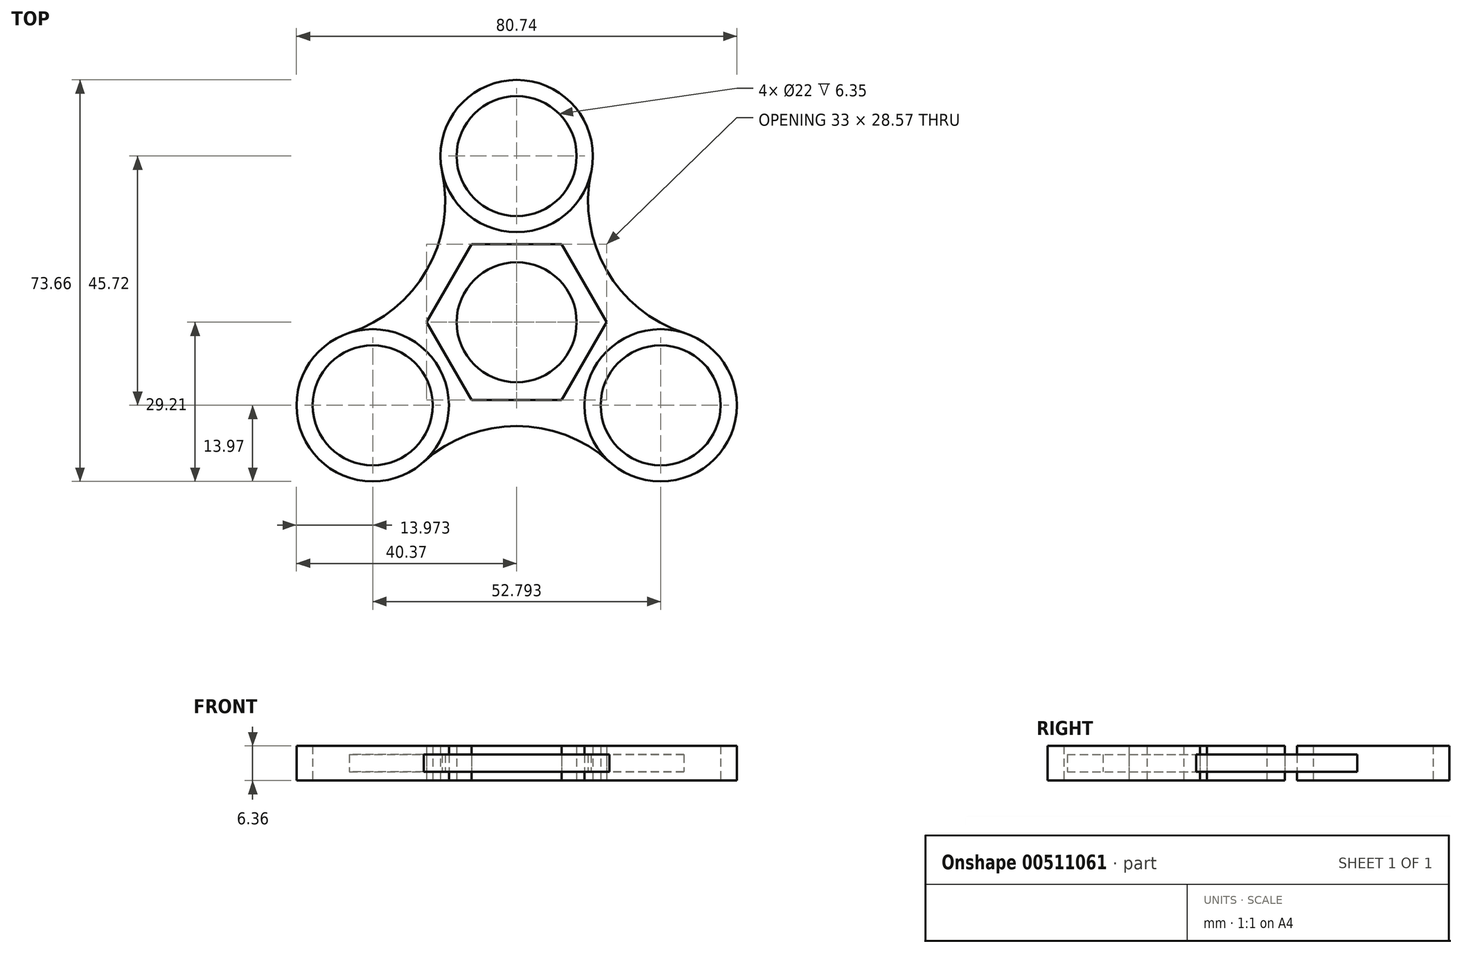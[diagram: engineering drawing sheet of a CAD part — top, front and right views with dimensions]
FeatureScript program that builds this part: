
annotation { "Feature Type Name" : "Feature", "Feature Type Description" : "" }
export const myFeature = defineFeature(function(context is Context, id is Id, definition is map)
    precondition{}
    {
        {
            var Q0;
            Q0=qCreatedBy(makeId("Top.planeOp"),FACE);
            var sketch = newSketch(context, id + "F0", { "sketchPlane" : qUnion([Q0])});
            skCircle(sketch, "E0", {"center": v(0, 0) * mm, "radius": 11 * mm});
            skCircle(sketch, "E1", {"center": v(0, 0) * mm, "radius": 44.45 * mm});
            skCircle(sketch, "E2", {"center": v(0, 30.48) * mm, "radius": 11 * mm});
            skCircle(sketch, "E3.1.0", {"center": v(-26.4, -15.24) * mm, "radius": 11 * mm});
            skCircle(sketch, "E3.2.0", {"center": v(26.4, -15.24) * mm, "radius": 11 * mm});
            skCircle(sketch, "E4", {"center": v(0, 30.48) * mm, "radius": 13.97 * mm});
            skCircle(sketch, "E5", {"center": v(26.4, -15.24) * mm, "radius": 13.97 * mm});
            skCircle(sketch, "E6", {"center": v(-26.4, -15.24) * mm, "radius": 13.97 * mm});
            skCircle(sketch, "E7.cCircle", {"center": v(0, 0) * mm, "radius": 14.29 * mm, "construction": true});
            skLineSegment(sketch, "E7.0", {"start": v(-8.25, 14.29) * mm, "end": v(8.25, 14.29) * mm});
            skLineSegment(sketch, "E7.1", {"start": v(8.25, 14.29) * mm, "end": v(16.5, 0) * mm});
            skLineSegment(sketch, "E7.2", {"start": v(16.5, 0) * mm, "end": v(8.25, -14.29) * mm});
            skLineSegment(sketch, "E7.3", {"start": v(8.25, -14.29) * mm, "end": v(-8.25, -14.29) * mm});
            skLineSegment(sketch, "E7.4", {"start": v(-8.25, -14.29) * mm, "end": v(-16.5, 0) * mm});
            skLineSegment(sketch, "E7.5", {"start": v(-16.5, 0) * mm, "end": v(-8.25, 14.29) * mm});
            skPoint(sketch, "E7.0.midPoint", {"position": v(0, 14.29) * mm});
            skSolve(sketch);
        }
        {
            var Q0;
            Q0=makeQuery(id+"F0.imprint","IMPRINT",FACE,{"disambiguationData":[TD([[makeQuery(id+"F0.imprint","IMPRINT",EDGE,{"derivedFrom":sQuery(id+"F0.wireOp",EDGE,"E2")}),-1.0]])]});
            var Q1;
            Q1=makeQuery(id+"F0.imprint","IMPRINT",FACE,{"disambiguationData":[TD([[makeQuery(id+"F0.imprint","IMPRINT",EDGE,{"derivedFrom":sQuery(id+"F0.wireOp",EDGE,"E0")}),-1.0]])]});
            var Q2;
            Q2=makeQuery(id+"F0.imprint","IMPRINT",FACE,{"disambiguationData":[TD([[makeQuery(id+"F0.imprint","IMPRINT",EDGE,{"derivedFrom":sQuery(id+"F0.wireOp",EDGE,"E3.1.0")}),-1.0]])]});
            var Q3;
            Q3=makeQuery(id+"F0.imprint","IMPRINT",FACE,{"disambiguationData":[TD([[makeQuery(id+"F0.imprint","IMPRINT",EDGE,{"derivedFrom":sQuery(id+"F0.wireOp",EDGE,"E3.2.0")}),-1.0]])]});
            extrude(context, id + "F1", {"entities" : qUnion([Q0, Q1, Q2, Q3]), "depth" : 3.17 * mm, "offsetDistance" : 25.4 * mm, "hasSecondDirection" : true, "secondDirectionOppositeDirection" : true, "secondDirectionDepth" : 3.17 * mm});
        }
        {
            var Q0;
            Q0=qCreatedBy(makeId("Top.planeOp"),FACE);
            var sketch = newSketch(context, id + "F2", { "sketchPlane" : qUnion([Q0])});
            skCircle(sketch, "E8.0", {"center": v(0, 30.48) * mm, "radius": 13.97 * mm});
            skLineSegment(sketch, "E9.0", {"start": v(-16.5, 0) * mm, "end": v(-8.25, 14.29) * mm});
            skLineSegment(sketch, "E10.0", {"start": v(-8.25, 14.29) * mm, "end": v(8.25, 14.29) * mm});
            skLineSegment(sketch, "E11.0", {"start": v(8.25, 14.29) * mm, "end": v(16.5, 0) * mm});
            skLineSegment(sketch, "E12.0", {"start": v(16.5, 0) * mm, "end": v(8.25, -14.29) * mm});
            skLineSegment(sketch, "E13.0", {"start": v(8.25, -14.29) * mm, "end": v(-8.25, -14.29) * mm});
            skLineSegment(sketch, "E14.0", {"start": v(-8.25, -14.29) * mm, "end": v(-16.5, 0) * mm});
            skCircle(sketch, "E15.0", {"center": v(-26.4, -15.24) * mm, "radius": 13.97 * mm});
            skCircle(sketch, "E16.0", {"center": v(26.4, -15.24) * mm, "radius": 13.97 * mm});
            skArc(sketch, "E17", {"start": v(-30.69, -1.95) * mm, "mid": v(-16.5, 9.53) * mm, "end": v(-13.66, 27.55) * mm});
            skArc(sketch, "E18", {"start": v(13.66, 27.55) * mm, "mid": v(16.5, 9.53) * mm, "end": v(30.69, -1.95) * mm});
            skArc(sketch, "E19", {"start": v(17.03, -25.6) * mm, "mid": v(0, -19.05) * mm, "end": v(-17.03, -25.6) * mm});
            skSolve(sketch);
        }
        {
            var Q0;
            Q0=makeQuery(id+"F2.imprint","IMPRINT",FACE,{"disambiguationData":[TD([[makeQuery(id+"F2.imprint","IMPRINT",EDGE,{"derivedFrom":sQuery(id+"F2.wireOp",EDGE,"E9.0")}),1.0]])]});
            extrude(context, id + "F3", {"entities" : qUnion([Q0]), "depth" : 1.59 * mm, "offsetDistance" : 25.4 * mm, "hasSecondDirection" : true, "secondDirectionOppositeDirection" : true, "secondDirectionDepth" : 1.59 * mm});
        }
    });
